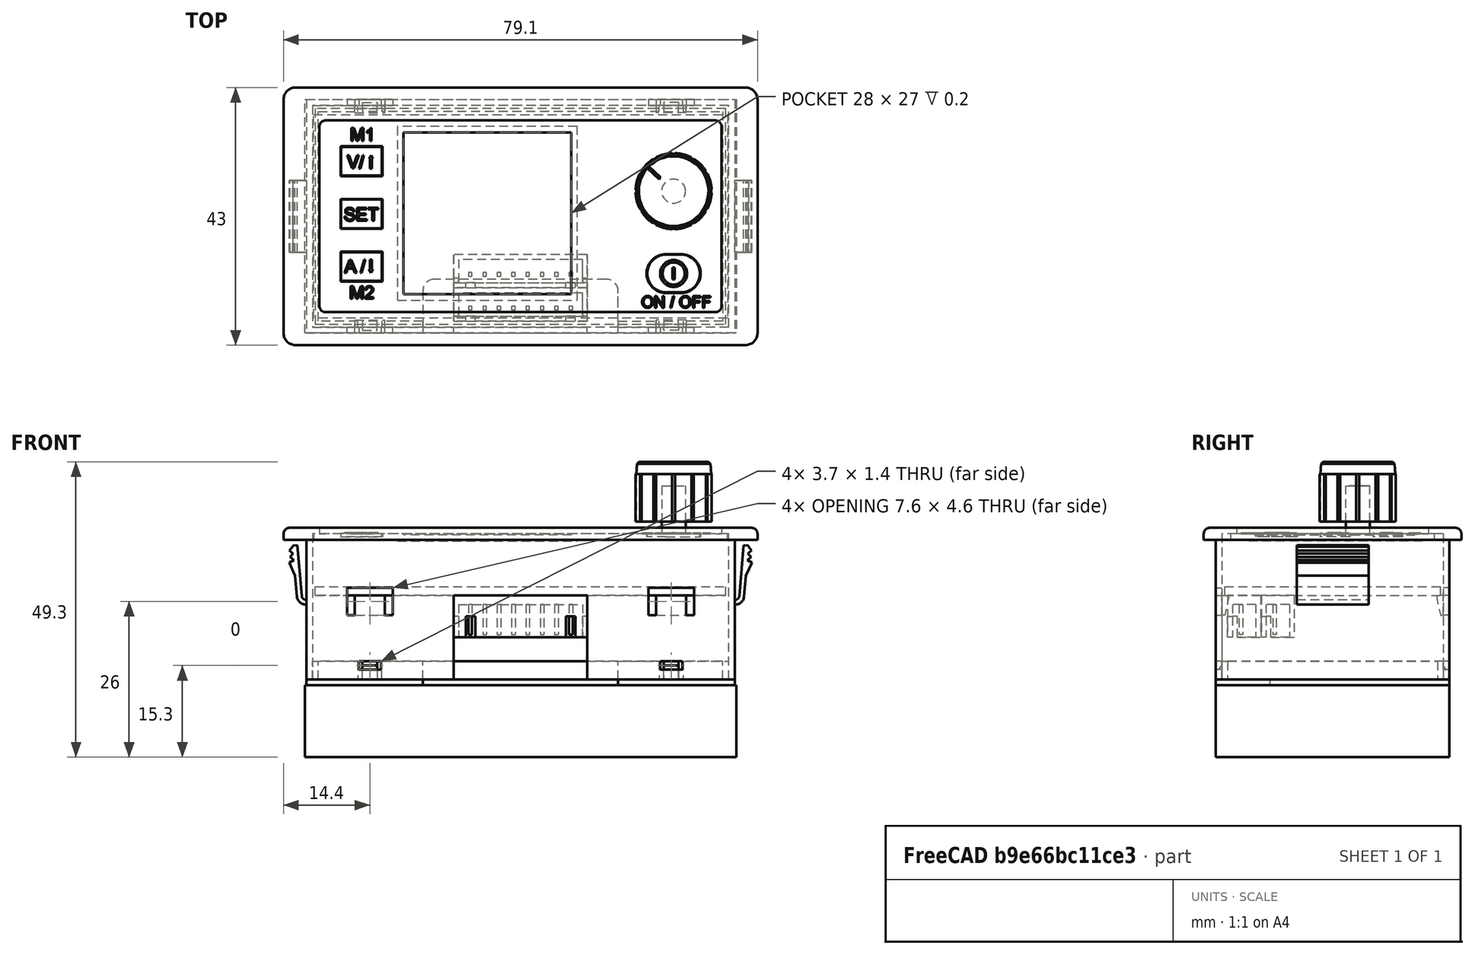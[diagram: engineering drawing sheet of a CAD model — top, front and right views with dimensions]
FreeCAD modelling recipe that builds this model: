
FCSTD DOCUMENT  (FreeCAD 0.18R4 (GitTag))
Label: dps-5015_001
License: Public Domain
LicenseURL: http://en.wikipedia.org/wiki/Public_domain
objects: Part::Feature×6, App::Part×3, Sketcher::SketchObject×1, PartDesign::Pad×1, PartDesign::Body×1
note: 10 computed .brp shape members not serialized (recipe doc carries the construction recipe); baked Part::Feature solids carry a one-line shape summary decoded from their .brp

FEATURE [Part::Feature] Part__Feature  label="Component4"
  shape: bbox 71.5 x 39 x 4 mm, 75 faces (baked)
FEATURE [Part::Feature] Part__Feature001  label="Component5"
  shape: bbox 79.1 x 43 x 32.3 mm, 446 faces (baked)
FEATURE [App::Part] Component1
  Group = -> [Part__Feature,Part__Feature001]
  Origin = -> Origin002
FEATURE [Part::Feature] Part__Feature002  label="Component6"
  shape: bbox 22.3 x 5.5 x 7 mm, 64 faces (baked)
FEATURE [Part::Feature] Part__Feature003  label="Component007"
  Placement = pos=(0,5.6,0) rot=(0,0,1;0rad)
  shape: bbox 22.3 x 5.5 x 7 mm, 64 faces (baked)
FEATURE [Part::Feature] Part__Feature004  label="SOLID"
  shape: bbox 68.5 x 36 x 1.5 mm, 6 faces (baked)
FEATURE [App::Part] Component2
  Group = -> [Part__Feature002,Part__Feature003,Part__Feature004]
  Origin = -> Origin003
FEATURE [Part::Feature] Part__Feature005  label="Component3"
  shape: bbox 12.7 x 12.7 x 10.01 mm, 70 faces (baked)
FEATURE [Sketcher::SketchObject] Sketch
  MapMode = 5
  Support = -> [XY_Plane004]
  sketch-geometry (4):
    g0: LineSegment StartX=-36 StartY=19.5 StartZ=0 EndX=36 EndY=19.5 EndZ=0
    g1: LineSegment StartX=36 StartY=19.5 StartZ=0 EndX=36 EndY=-19.5 EndZ=0
    g2: LineSegment StartX=36 StartY=-19.5 StartZ=0 EndX=-36 EndY=-19.5 EndZ=0
    g3: LineSegment StartX=-36 StartY=-19.5 StartZ=0 EndX=-36 EndY=19.5 EndZ=0
  constraints (11):
    c: Coincident(g0,g1)
    c: Coincident(g1,g2)
    c: Coincident(g2,g3)
    c: Coincident(g3,g0)
    c: Horizontal(g0)
    c: Horizontal(g2)
    c: Vertical(g1)
    c: Vertical(g3)
    c: DistanceY(g1,g1) = 39
    c: DistanceX(g2,g2) = 72
    c: Symmetric(g0,g1,g-1)
FEATURE [PartDesign::Pad] Pad
  Length = 12
  Length2 = 100
  Profile = -> Sketch
  Reversed = true
  Type = 0
FEATURE [PartDesign::Body] Body  label="zoneInterdite"
  Group = -> [Sketch,Pad]
  Origin = -> Origin
  Tip = -> Pad
FEATURE [App::Part] DPS_5015_display_v20  label="DPS 3005isplay v20"
  Group = -> [Component1,Component2,Part__Feature005,Body]
  Origin = -> Origin004
